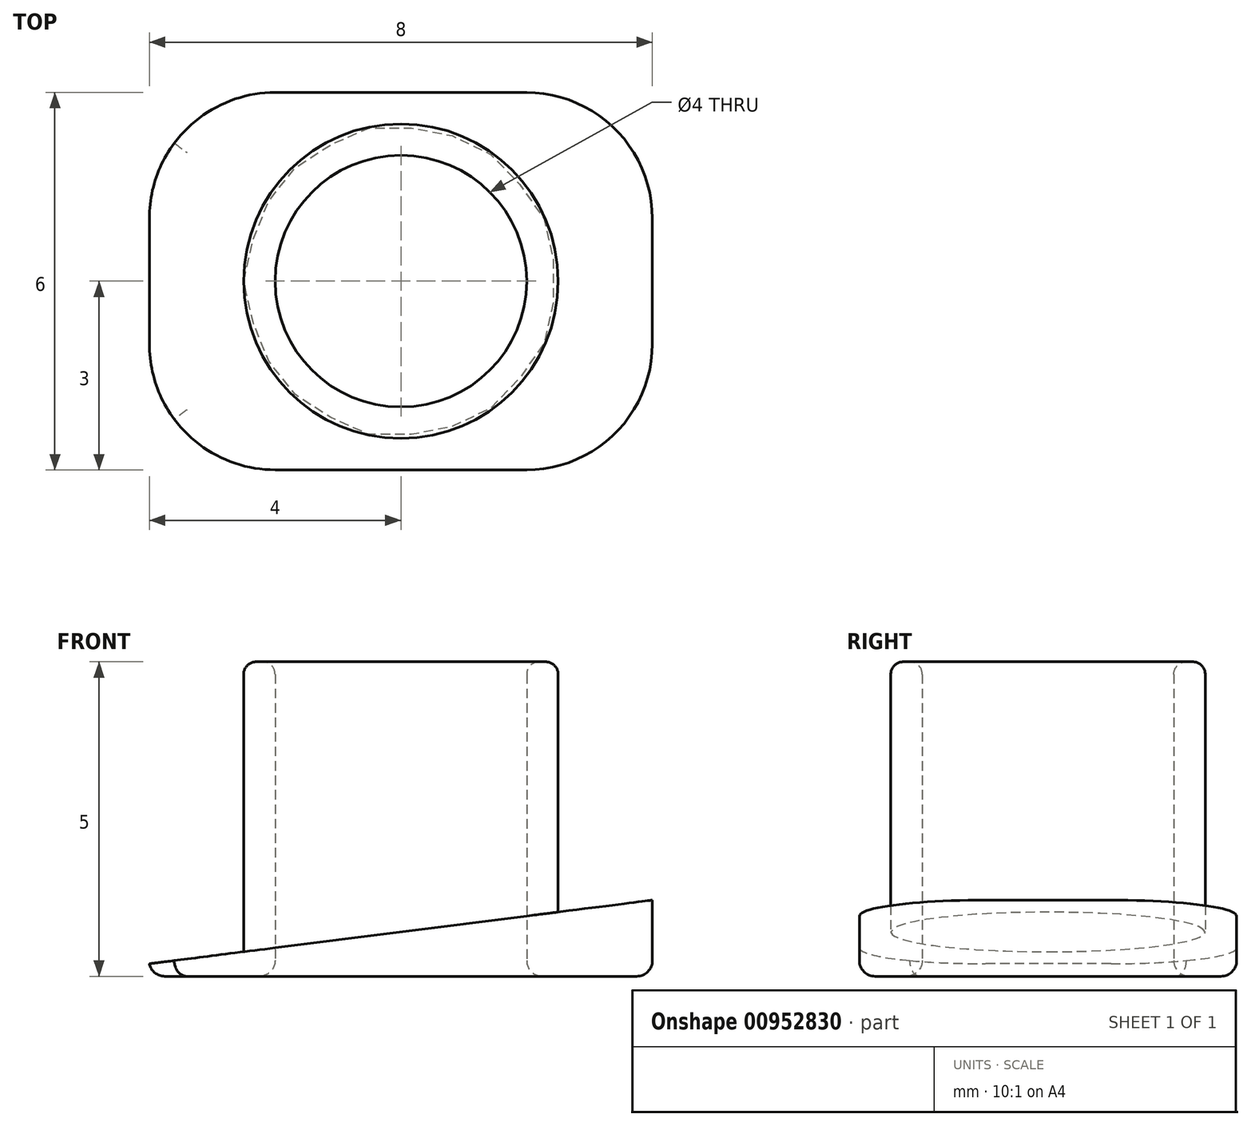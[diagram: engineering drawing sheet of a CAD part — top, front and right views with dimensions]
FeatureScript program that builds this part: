
annotation { "Feature Type Name" : "Feature", "Feature Type Description" : "" }
export const myFeature = defineFeature(function(context is Context, id is Id, definition is map)
    precondition{}
    {
        {
            var Q0;
            Q0=qCreatedBy(makeId("Top.planeOp"),FACE);
            var sketch = newSketch(context, id + "F0", { "sketchPlane" : qUnion([Q0])});
            skCircle(sketch, "E0", {"center": v(0, 0) * mm, "radius": 2.5 * mm});
            skCircle(sketch, "E1", {"center": v(0, 0) * mm, "radius": 2 * mm});
            skLineSegment(sketch, "E2.bottom", {"start": v(-4, 3) * mm, "end": v(4, 3) * mm});
            skLineSegment(sketch, "E2.top", {"start": v(-4, -3) * mm, "end": v(4, -3) * mm});
            skLineSegment(sketch, "E2.left", {"start": v(-4, 3) * mm, "end": v(-4, -3) * mm});
            skLineSegment(sketch, "E2.right", {"start": v(4, 3) * mm, "end": v(4, -3) * mm});
            skSolve(sketch);
        }
        {
            var Q0;
            Q0=makeQuery(id+"F0.imprint","IMPRINT",FACE,{"disambiguationData":[TD([[makeQuery(id+"F0.imprint","IMPRINT",EDGE,{"derivedFrom":sQuery(id+"F0.wireOp",EDGE,"E0")}),-1.0]])]});
            extrude(context, id + "F1", {"entities" : qUnion([Q0]), "depth" : 5 * mm, "offsetDistance" : 25 * mm});
        }
        {
            var Q0;
            Q0=makeQuery(id+"F1.opExtrude","SWEPT_FACE",FACE,{"disambiguationData":[OSD([sQuery(id+"F0.wireOp",EDGE,"E2.top")])]});
            var sketch = newSketch(context, id + "F2", { "sketchPlane" : qUnion([Q0])});
            skPoint(sketch, "E3.0", {"position": v(-4, 0) * mm});
            skPoint(sketch, "E4.0", {"position": v(4, 0) * mm});
            skLineSegment(sketch, "E5", {"start": v(-4, 0) * mm, "end": v(-4, 0.2) * mm});
            skLineSegment(sketch, "E6", {"start": v(-4, 0.2) * mm, "end": v(4, 1.21) * mm});
            skLineSegment(sketch, "E7", {"start": v(4, 1.21) * mm, "end": v(4, 0) * mm});
            skLineSegment(sketch, "E8", {"start": v(-4, 0.2) * mm, "end": v(-4, 5) * mm});
            skLineSegment(sketch, "E9", {"start": v(-4, 5) * mm, "end": v(4, 5) * mm});
            skLineSegment(sketch, "E10", {"start": v(4, 5) * mm, "end": v(4, 1.21) * mm});
            skSolve(sketch);
        }
        {
            var Q0;
            Q0=makeQuery(id+"F2.imprint","IMPRINT",FACE,{"disambiguationData":[TD([[makeQuery(id+"F2.imprint","IMPRINT",EDGE,{"derivedFrom":sQuery(id+"F2.wireOp",EDGE,"E6")}),1.0]])]});
            extrude(context, id + "F3", {"entities" : qUnion([Q0]), "operationType" : NewBodyOperationType.REMOVE, "oppositeDirection" : true, "depth" : 25 * mm, "offsetDistance" : 25 * mm});
        }
        {
            var Q0;
            Q0=makeQuery(id+"F0.imprint","IMPRINT",FACE,{"disambiguationData":[TD([[makeQuery(id+"F0.imprint","IMPRINT",EDGE,{"derivedFrom":sQuery(id+"F0.wireOp",EDGE,"E0")}),1.0]])]});
            extrude(context, id + "F4", {"entities" : qUnion([Q0]), "operationType" : NewBodyOperationType.ADD, "depth" : 5 * mm, "offsetDistance" : 25 * mm});
        }
        {
            var Q0;
            Q0=makeQuery(id+"F1.opExtrude","SWEPT_EDGE",EDGE,{"disambiguationData":[OSD([sQuery(id+"F0.wireOp",EDGE,"E2.bottom"),sQuery(id+"F0.wireOp",EDGE,"E2.right")])]});
            var Q1;
            Q1=makeQuery(id+"F1.opExtrude","SWEPT_EDGE",EDGE,{"disambiguationData":[OSD([sQuery(id+"F0.wireOp",EDGE,"E2.bottom"),sQuery(id+"F0.wireOp",EDGE,"E2.left")])]});
            var Q2;
            Q2=makeQuery(id+"F1.opExtrude","SWEPT_EDGE",EDGE,{"disambiguationData":[OSD([sQuery(id+"F0.wireOp",EDGE,"E2.top"),sQuery(id+"F0.wireOp",EDGE,"E2.left")])]});
            var Q3;
            Q3=makeQuery(id+"F1.opExtrude","SWEPT_EDGE",EDGE,{"disambiguationData":[OSD([sQuery(id+"F0.wireOp",EDGE,"E2.top"),sQuery(id+"F0.wireOp",EDGE,"E2.right")])]});
            fillet(context, id + "F5", {"entities" : qUnion([Q0, Q1, Q2, Q3]), "radius" : 2 * mm, "tangentPropagation" : true, "allowEdgeOverflow" : false});
        }
        {
            var Q0;
            {var subQ0=sQuery(id+"F0.wireOp",EDGE,"E0");Q0=makeQuery(id+"F4.boolean.opBoolean","MERGE",FACE,{"derivedFrom":[makeQuery(id+"F1.opExtrude","CAP_FACE",FACE,{"disambiguationData":[OSD([subQ0,sQuery(id+"F0.wireOp",EDGE,"E2.bottom"),sQuery(id+"F0.wireOp",EDGE,"E2.top"),sQuery(id+"F0.wireOp",EDGE,"E2.left"),sQuery(id+"F0.wireOp",EDGE,"E2.right")])],"isStart":true}),makeQuery(id+"F4.opExtrude","CAP_FACE",FACE,{"disambiguationData":[OSD([subQ0,sQuery(id+"F0.wireOp",EDGE,"E1")])],"isStart":true})]});}
            fillet(context, id + "F6", {"entities" : qUnion([Q0]), "radius" : 0.25 * mm, "tangentPropagation" : true, "allowEdgeOverflow" : false});
        }
        {
            var Q0;
            Q0=makeQuery(id+"F4.opExtrude","CAP_EDGE",EDGE,{"disambiguationData":[OSD([sQuery(id+"F0.wireOp",EDGE,"E1")])],"isStart":false});
            var Q1;
            Q1=makeQuery(id+"F4.opExtrude","CAP_EDGE",EDGE,{"disambiguationData":[OSD([sQuery(id+"F0.wireOp",EDGE,"E0")])],"isStart":false});
            fillet(context, id + "F7", {"entities" : qUnion([Q0, Q1]), "radius" : 0.2 * mm, "tangentPropagation" : true, "allowEdgeOverflow" : false});
        }
    });
